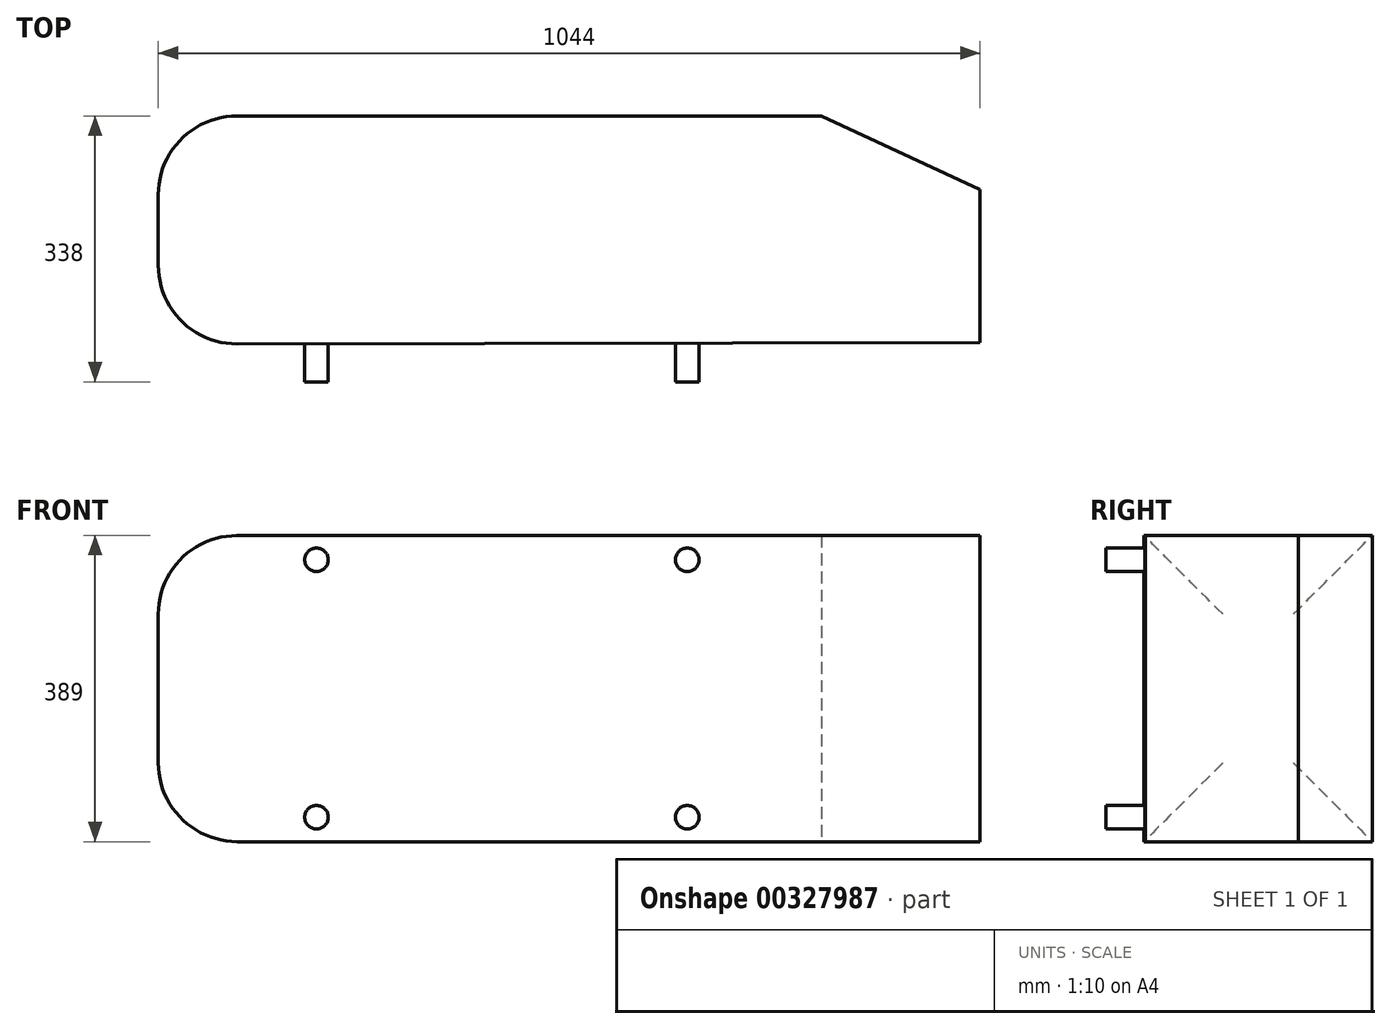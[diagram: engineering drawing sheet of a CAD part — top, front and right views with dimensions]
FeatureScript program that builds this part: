
annotation { "Feature Type Name" : "Feature", "Feature Type Description" : "" }
export const myFeature = defineFeature(function(context is Context, id is Id, definition is map)
    precondition{}
    {
        {
            var Q0;
            Q0=qCreatedBy(makeId("Top.planeOp"),FACE);
            var sketch = newSketch(context, id + "F0", { "sketchPlane" : qUnion([Q0])});
            skLineSegment(sketch, "E0", {"start": v(0, 0) * mm, "end": v(0, 50) * mm, "construction": true});
            skLineSegment(sketch, "E1", {"start": v(0, 50) * mm, "end": v(-1044, 48) * mm});
            skLineSegment(sketch, "E2", {"start": v(-1044, 48) * mm, "end": v(-1044, 50) * mm});
            skLineSegment(sketch, "E3", {"start": v(-1044, 50) * mm, "end": v(-1044, 338) * mm});
            skLineSegment(sketch, "E4", {"start": v(0, 50) * mm, "end": v(0, 244.18) * mm});
            skLineSegment(sketch, "E5", {"start": v(-1044, 338) * mm, "end": v(231.64, 338) * mm, "construction": true});
            skLineSegment(sketch, "E6", {"start": v(-1044, 338) * mm, "end": v(-201.2, 338) * mm});
            skLineSegment(sketch, "E7", {"start": v(0, 244.18) * mm, "end": v(-201.2, 338) * mm});
            skSolve(sketch);
        }
        {
            var Q0;
            Q0=makeQuery(id+"F0.imprint","IMPRINT",FACE,{"disambiguationData":[TD([[makeQuery(id+"F0.imprint","IMPRINT",EDGE,{"derivedFrom":sQuery(id+"F0.wireOp",EDGE,"E1")}),-1.0]])]});
            extrude(context, id + "F1", {"entities" : qUnion([Q0]), "depth" : (389 / 2) * mm});
        }
        {
            var Q0;
            Q0 = qSketchRegion(id + "F0", true);
            extrude(context, id + "F2", {"entities" : qUnion([Q0]), "operationType" : NewBodyOperationType.ADD, "oppositeDirection" : true, "depth" : (389 / 2) * mm});
        }
        {
            var Q0;
            Q0=qCreatedBy(makeId("Front.planeOp"),FACE);
            var sketch = newSketch(context, id + "F3", { "sketchPlane" : qUnion([Q0])});
            skLineSegment(sketch, "E8", {"start": v(0, 0) * mm, "end": v(-372, 0) * mm, "construction": true});
            skLineSegment(sketch, "E9", {"start": v(-372, 0) * mm, "end": v(-843, 0) * mm, "construction": true});
            skLineSegment(sketch, "E10", {"start": v(-843, 0) * mm, "end": v(-843, -163.5) * mm, "construction": true});
            skLineSegment(sketch, "E11.MirrorCS", {"start": v(-843, 0) * mm, "end": v(-843, 163.5) * mm, "construction": true});
            skLineSegment(sketch, "E12", {"start": v(-372, 0) * mm, "end": v(-372, -163.5) * mm, "construction": true});
            skLineSegment(sketch, "E13.MirrorCS", {"start": v(-372, 0) * mm, "end": v(-372, 163.5) * mm, "construction": true});
            skCircle(sketch, "E14", {"center": v(-843, 163.5) * mm, "radius": 15 * mm});
            skCircle(sketch, "E15.MirrorC", {"center": v(-843, -163.5) * mm, "radius": 15 * mm});
            skCircle(sketch, "E16", {"center": v(-372, 163.5) * mm, "radius": 15 * mm});
            skCircle(sketch, "E17.MirrorC", {"center": v(-372, -163.5) * mm, "radius": 15 * mm});
            skSolve(sketch);
        }
        {
            var Q0;
            Q0 = qSketchRegion(id + "F3", true);
            extrude(context, id + "F4", {"entities" : qUnion([Q0]), "endBound" : BoundingType.UP_TO_NEXT, "oppositeDirection" : true, "depth" : 25 * mm});
        }
        {
            var Q0;
            {var subQ0=sQuery(id+"F0.wireOp",EDGE,"E3");var subQ1=sQuery(id+"F0.wireOp",EDGE,"E2");Q0=makeQuery(id+"F2.boolean.opBoolean","MERGE",FACE,{"derivedFrom":[makeQuery(id+"F1.opExtrude","SWEPT_FACE",FACE,{"disambiguationData":[OSD([subQ1,subQ0])]}),makeQuery(id+"F2.opExtrude","SWEPT_FACE",FACE,{"disambiguationData":[OSD([subQ1,subQ0])]})]});}
            fillet(context, id + "F5", {"entities" : qUnion([Q0]), "radius" : 100 * mm, "tangentPropagation" : true, "allowEdgeOverflow" : false});
        }
    });
